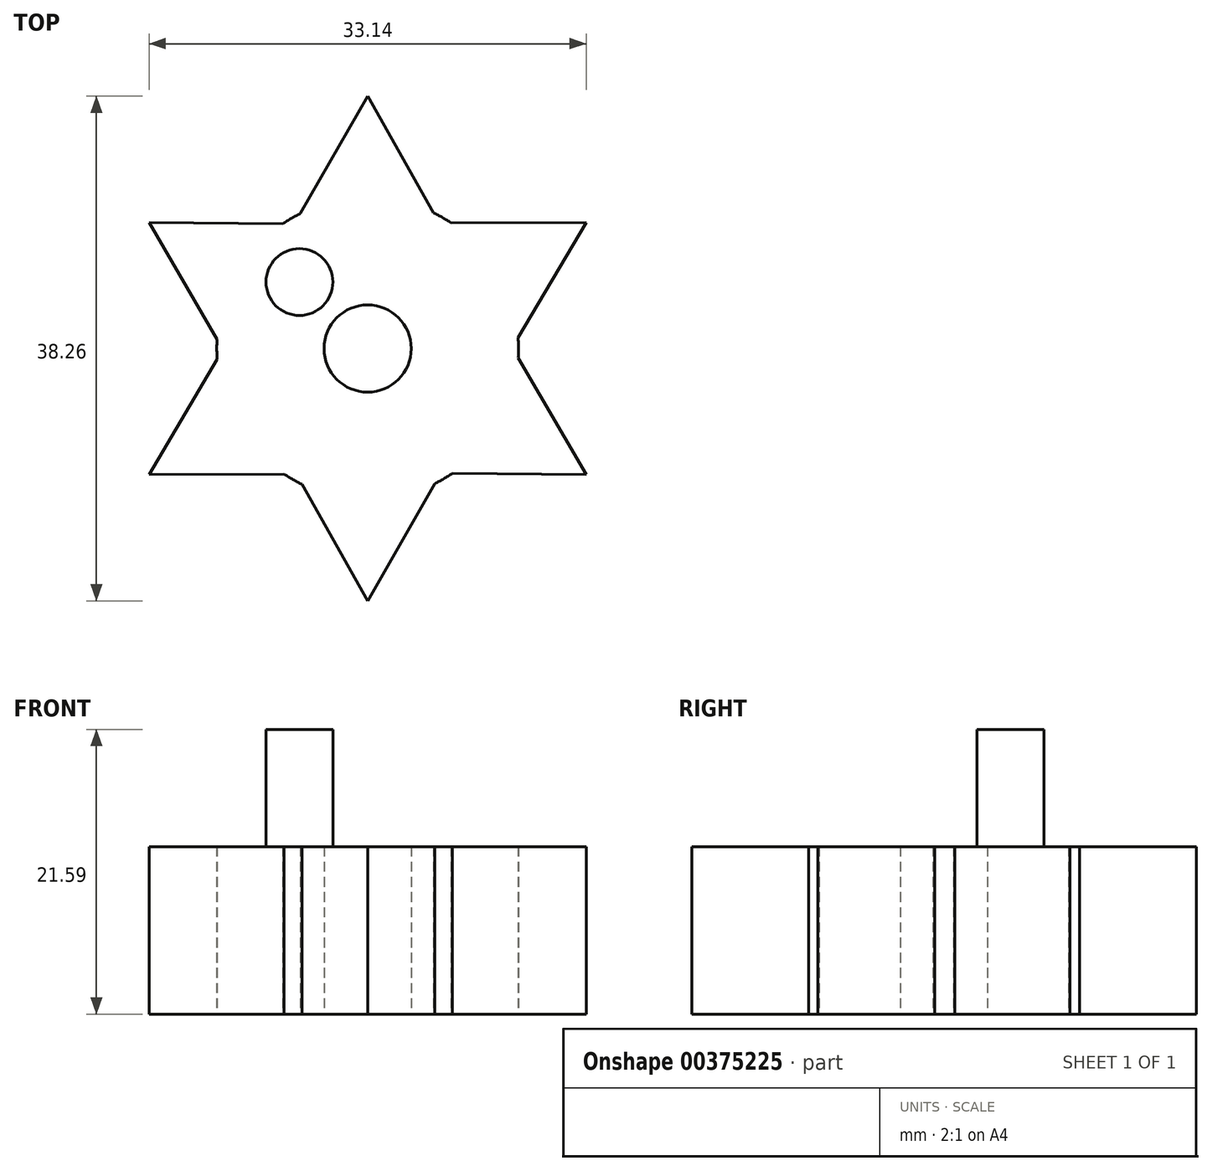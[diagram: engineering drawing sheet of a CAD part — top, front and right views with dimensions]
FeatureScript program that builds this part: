
annotation { "Feature Type Name" : "Feature", "Feature Type Description" : "" }
export const myFeature = defineFeature(function(context is Context, id is Id, definition is map)
    precondition{}
    {
        {
            var Q0;
            Q0=qCreatedBy(makeId("Top.planeOp"),FACE);
            var sketch = newSketch(context, id + "F0", { "sketchPlane" : qUnion([Q0])});
            skCircle(sketch, "E0", {"center": v(0, 0) * mm, "radius": 11.44 * mm});
            skLineSegment(sketch, "E1", {"start": v(0, 11.44) * mm, "end": v(0, 19.13) * mm});
            skLineSegment(sketch, "E2", {"start": v(0, 19.13) * mm, "end": v(4.98, 10.3) * mm});
            skLineSegment(sketch, "E3", {"start": v(0, 19.13) * mm, "end": v(-5.1, 10.24) * mm});
            skLineSegment(sketch, "E4.1.0", {"start": v(-16.57, 9.57) * mm, "end": v(-6.43, 9.46) * mm});
            skLineSegment(sketch, "E4.1.1", {"start": v(-16.57, 9.57) * mm, "end": v(-11.42, 0.71) * mm});
            skLineSegment(sketch, "E4.2.0", {"start": v(-16.57, -9.57) * mm, "end": v(-11.4, -0.83) * mm});
            skLineSegment(sketch, "E4.2.1", {"start": v(-16.57, -9.57) * mm, "end": v(-6.33, -9.53) * mm});
            skLineSegment(sketch, "E4.3.0", {"start": v(0, -19.13) * mm, "end": v(-4.98, -10.3) * mm});
            skLineSegment(sketch, "E4.3.1", {"start": v(0, -19.13) * mm, "end": v(5.1, -10.24) * mm});
            skLineSegment(sketch, "E4.4.0", {"start": v(16.57, -9.57) * mm, "end": v(6.43, -9.46) * mm});
            skLineSegment(sketch, "E4.4.1", {"start": v(16.57, -9.57) * mm, "end": v(11.42, -0.71) * mm});
            skLineSegment(sketch, "E4.5.0", {"start": v(16.57, 9.57) * mm, "end": v(11.4, 0.83) * mm});
            skLineSegment(sketch, "E4.5.1", {"start": v(16.57, 9.57) * mm, "end": v(6.33, 9.53) * mm});
            skCircle(sketch, "E5", {"center": v(0, 0) * mm, "radius": 3.3 * mm});
            skSolve(sketch);
        }
        {
            var Q0;
            Q0 = qSketchRegion(id + "F0", true);
            extrude(context, id + "F1", {"entities" : qUnion([Q0]), "depth" : 12.7 * mm});
        }
        {
            var Q0;
            Q0=makeQuery(id+"F1.opExtrude","CAP_FACE",FACE,{"disambiguationData":[OSD([sQuery(id+"F0.wireOp",EDGE,"E0"),sQuery(id+"F0.wireOp",EDGE,"E2"),sQuery(id+"F0.wireOp",EDGE,"E3"),sQuery(id+"F0.wireOp",EDGE,"E4.1.0"),sQuery(id+"F0.wireOp",EDGE,"E4.1.1"),sQuery(id+"F0.wireOp",EDGE,"E4.2.0"),sQuery(id+"F0.wireOp",EDGE,"E4.2.1"),sQuery(id+"F0.wireOp",EDGE,"E4.3.0"),sQuery(id+"F0.wireOp",EDGE,"E4.3.1"),sQuery(id+"F0.wireOp",EDGE,"E4.4.0"),sQuery(id+"F0.wireOp",EDGE,"E4.4.1"),sQuery(id+"F0.wireOp",EDGE,"E4.5.0"),sQuery(id+"F0.wireOp",EDGE,"E4.5.1"),sQuery(id+"F0.wireOp",EDGE,"E5")])],"isStart":false});
            var sketch = newSketch(context, id + "F2", { "sketchPlane" : qUnion([Q0])});
            skCircle(sketch, "E6", {"center": v(-5.17, 5.04) * mm, "radius": 2.53 * mm});
            skSolve(sketch);
        }
        {
            var Q0;
            Q0=makeQuery(id+"F2.imprint","IMPRINT",FACE,{"disambiguationData":[TD([[makeQuery(id+"F2.imprint","IMPRINT",EDGE,{"derivedFrom":sQuery(id+"F2.wireOp",EDGE,"E6")}),1.0]])]});
            extrude(context, id + "F3", {"entities" : qUnion([Q0]), "operationType" : NewBodyOperationType.ADD, "depth" : 8.9 * mm});
        }
    });
